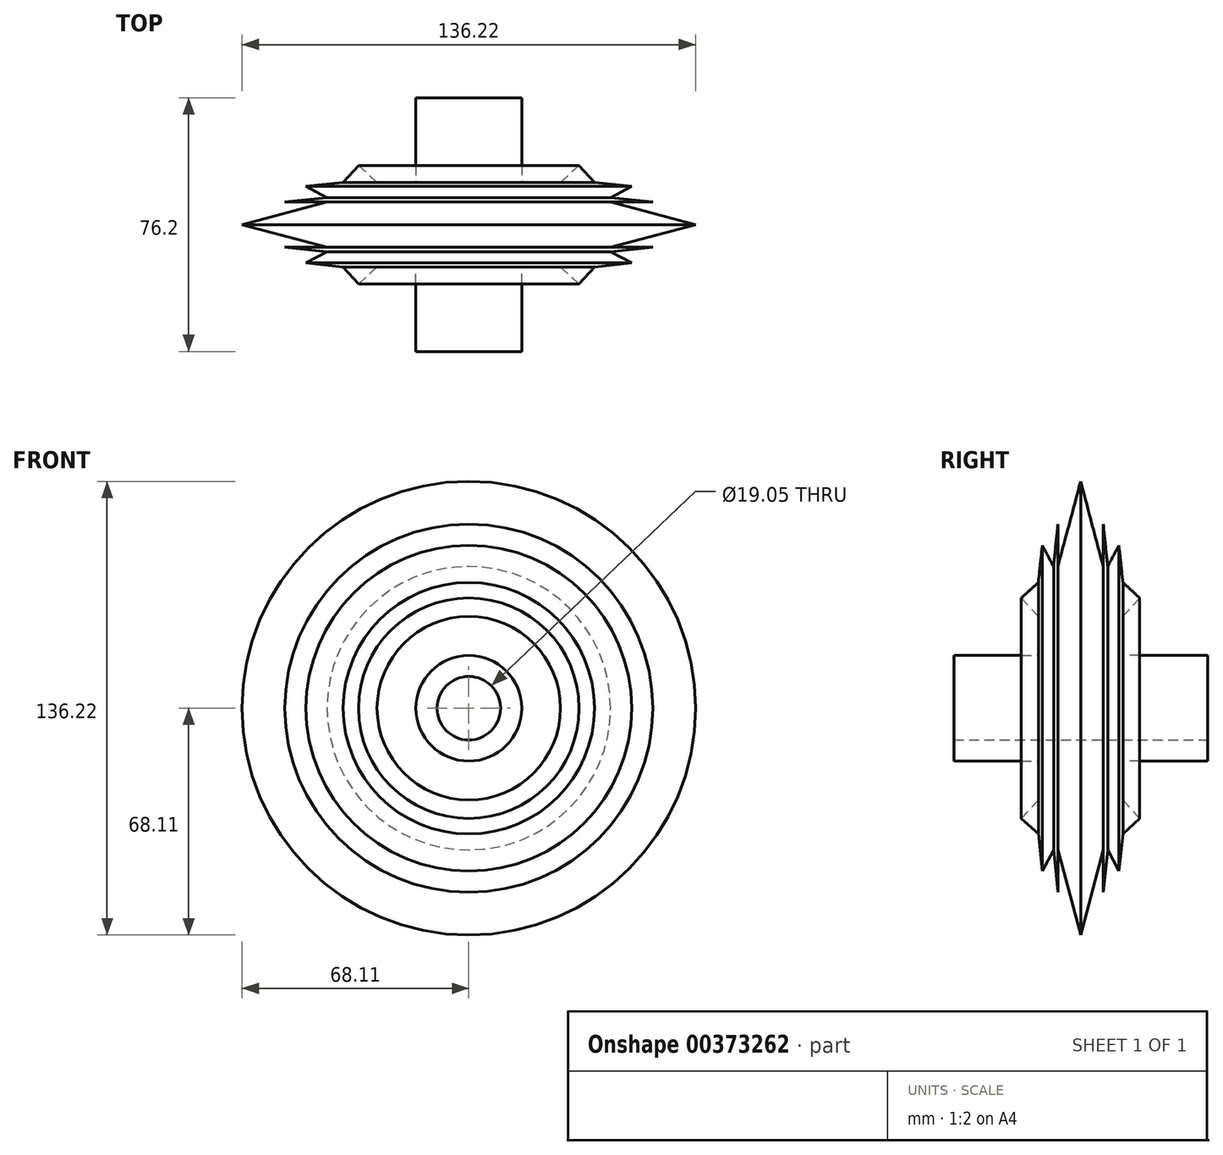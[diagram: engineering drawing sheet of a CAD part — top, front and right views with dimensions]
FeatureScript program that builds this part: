
annotation { "Feature Type Name" : "Feature", "Feature Type Description" : "" }
export const myFeature = defineFeature(function(context is Context, id is Id, definition is map)
    precondition{}
    {
        {
            var Q0;
            Q0=qCreatedBy(makeId("Front.planeOp"),FACE);
            var sketch = newSketch(context, id + "F0", { "sketchPlane" : qUnion([Q0])});
            skCircle(sketch, "E0", {"center": v(0, 0) * mm, "radius": 9.53 * mm});
            skCircle(sketch, "E1", {"center": v(0, 0) * mm, "radius": 15.88 * mm});
            skSolve(sketch);
        }
        {
            var Q0;
            Q0=makeQuery(id+"F0.imprint","IMPRINT",FACE,{"disambiguationData":[TD([[makeQuery(id+"F0.imprint","IMPRINT",EDGE,{"derivedFrom":sQuery(id+"F0.wireOp",EDGE,"E0")}),-1.0]])]});
            extrude(context, id + "F1", {"entities" : qUnion([Q0]), "depth" : 25.4 * mm});
        }
        {
            var Q0;
            Q0=qCreatedBy(makeId("Right.planeOp"),FACE);
            var sketch = newSketch(context, id + "F2", { "sketchPlane" : qUnion([Q0])});
            skLineSegment(sketch, "E2", {"start": v(-25.4, 15.88) * mm, "end": v(-25.4, -15.87) * mm});
            skLineSegment(sketch, "E3", {"start": v(-25.4, 15.87) * mm, "end": v(0, 15.87) * mm});
            skLineSegment(sketch, "E4", {"start": v(0, 15.87) * mm, "end": v(0, -16.16) * mm});
            skLineSegment(sketch, "E5", {"start": v(0, -16.16) * mm, "end": v(-25.4, -15.87) * mm});
            skLineSegment(sketch, "E6", {"start": v(0, -16.16) * mm, "end": v(0, 15.87) * mm});
            skLineSegment(sketch, "E7", {"start": v(-25.4, 9.85) * mm, "end": v(0, 9.85) * mm});
            skLineSegment(sketch, "E8", {"start": v(-25.4, 33.1) * mm, "end": v(-25.4, 9.85) * mm});
            skLineSegment(sketch, "E9", {"start": v(0, 33.1) * mm, "end": v(5.08, 33.1) * mm});
            skLineSegment(sketch, "E10", {"start": v(-25.4, 33.1) * mm, "end": v(-30.48, 33.1) * mm});
            skLineSegment(sketch, "E11", {"start": v(-30.48, 33.1) * mm, "end": v(-25.4, 37.76) * mm});
            skLineSegment(sketch, "E12", {"start": v(-25.4, 37.76) * mm, "end": v(-25.4, 33.1) * mm});
            skLineSegment(sketch, "E13", {"start": v(-30.48, 33.1) * mm, "end": v(-25.4, 27.56) * mm});
            skLineSegment(sketch, "E14", {"start": v(-25.4, 37.76) * mm, "end": v(-20.83, 42.57) * mm});
            skLineSegment(sketch, "E15", {"start": v(-20.83, 42.57) * mm, "end": v(-4.57, 42.57) * mm});
            skLineSegment(sketch, "E16", {"start": v(-20.83, 42.57) * mm, "end": v(-19.5, 55.27) * mm});
            skLineSegment(sketch, "E17", {"start": v(-19.5, 55.27) * mm, "end": v(-19.5, 42.57) * mm});
            skLineSegment(sketch, "E18", {"start": v(-20.83, 42.57) * mm, "end": v(-24.2, 48.92) * mm});
            skPoint(sketch, "E18.endSnap0", {"position": v(-20.17, 48.92) * mm});
            skLineSegment(sketch, "E19", {"start": v(-24.2, 48.92) * mm, "end": v(-25.4, 37.76) * mm});
            skLineSegment(sketch, "E20", {"start": v(-12.7, 42.57) * mm, "end": v(-12.7, 15.87) * mm});
            skLineSegment(sketch, "E21", {"start": v(-19.5, 42.57) * mm, "end": v(-12.7, 68.11) * mm});
            skLineSegment(sketch, "E22", {"start": v(-12.7, 42.57) * mm, "end": v(-12.7, 68.11) * mm});
            skLineSegment(sketch, "E23.MirrorCS", {"start": v(-5.9, 42.57) * mm, "end": v(-12.7, 68.11) * mm});
            skLineSegment(sketch, "E24.MirrorCS", {"start": v(-5.9, 55.27) * mm, "end": v(-5.9, 42.57) * mm});
            skLineSegment(sketch, "E25.MirrorCS", {"start": v(-4.57, 42.57) * mm, "end": v(-5.9, 55.27) * mm});
            skLineSegment(sketch, "E26.MirrorCS", {"start": v(-4.57, 42.57) * mm, "end": v(-1.2, 48.92) * mm});
            skLineSegment(sketch, "E27.MirrorCS", {"start": v(-1.2, 48.92) * mm, "end": v(0, 37.76) * mm});
            skLineSegment(sketch, "E28.MirrorCS", {"start": v(5.08, 33.1) * mm, "end": v(0, 37.76) * mm});
            skLineSegment(sketch, "E29.MirrorCS", {"start": v(5.08, 33.1) * mm, "end": v(0, 27.56) * mm});
            skLineSegment(sketch, "E30.MirrorCS", {"start": v(0, 33.1) * mm, "end": v(0, 9.85) * mm});
            skLineSegment(sketch, "E31.MirrorCS", {"start": v(0, 37.76) * mm, "end": v(0, 33.1) * mm});
            skSolve(sketch);
        }
        {
            var Q0;
            {var subQ0=sQuery(id+"F2.wireOp",EDGE,"E12");Q0=makeQuery(id+"F2.imprint","IMPRINT",FACE,{"disambiguationData":[TD([[makeQuery(id+"F2.imprint","IMPRINT",EDGE,{"derivedFrom":subQ0}),1.0]])]});}
            var Q1;
            {var subQ0=sQuery(id+"F2.wireOp",EDGE,"E20");Q1=makeQuery(id+"F2.imprint","IMPRINT",FACE,{"disambiguationData":[TD([[makeQuery(id+"F2.imprint","IMPRINT",EDGE,{"derivedFrom":subQ0}),1.0]])]});}
            var Q2;
            {var subQ0=sQuery(id+"F2.wireOp",EDGE,"E9");Q2=makeQuery(id+"F2.imprint","IMPRINT",FACE,{"disambiguationData":[TD([[makeQuery(id+"F2.imprint","IMPRINT",EDGE,{"derivedFrom":subQ0}),-1.0]])]});}
            var Q3;
            Q3=makeQuery(id+"F2.imprint","IMPRINT",FACE,{"disambiguationData":[TD([[makeQuery(id+"F2.imprint","IMPRINT",EDGE,{"derivedFrom":sQuery(id+"F2.wireOp",EDGE,"E9")}),1.0]])]});
            var Q4;
            {var subQ0=sQuery(id+"F2.wireOp",EDGE,"E10");Q4=makeQuery(id+"F2.imprint","IMPRINT",FACE,{"disambiguationData":[TD([[makeQuery(id+"F2.imprint","IMPRINT",EDGE,{"derivedFrom":subQ0}),1.0]])]});}
            var Q5;
            Q5=makeQuery(id+"F2.imprint","IMPRINT",FACE,{"disambiguationData":[TD([[makeQuery(id+"F2.imprint","IMPRINT",EDGE,{"derivedFrom":sQuery(id+"F2.wireOp",EDGE,"E10")}),-1.0]])]});
            var Q6;
            Q6=makeQuery(id+"F2.imprint","IMPRINT",FACE,{"disambiguationData":[TD([[makeQuery(id+"F2.imprint","IMPRINT",EDGE,{"derivedFrom":sQuery(id+"F2.wireOp",EDGE,"E14")}),1.0]])]});
            var Q7;
            {var subQ0=sQuery(id+"F2.wireOp",EDGE,"E16");Q7=makeQuery(id+"F2.imprint","IMPRINT",FACE,{"disambiguationData":[TD([[makeQuery(id+"F2.imprint","IMPRINT",EDGE,{"derivedFrom":subQ0}),-1.0]])]});}
            var Q8;
            {var subQ0=sQuery(id+"F2.wireOp",EDGE,"E21");Q8=makeQuery(id+"F2.imprint","IMPRINT",FACE,{"disambiguationData":[TD([[makeQuery(id+"F2.imprint","IMPRINT",EDGE,{"derivedFrom":subQ0}),-1.0]])]});}
            var Q9;
            {var subQ0=sQuery(id+"F2.wireOp",EDGE,"E22");Q9=makeQuery(id+"F2.imprint","IMPRINT",FACE,{"disambiguationData":[TD([[makeQuery(id+"F2.imprint","IMPRINT",EDGE,{"derivedFrom":subQ0}),-1.0]])]});}
            var Q10;
            {var subQ2=sQuery(id+"F2.wireOp",EDGE,"E24.MirrorCS");Q10=makeQuery(id+"F2.imprint","IMPRINT",FACE,{"disambiguationData":[TD([[makeQuery(id+"F2.imprint","IMPRINT",EDGE,{"derivedFrom":subQ2}),1.0]])]});}
            var Q11;
            Q11=makeQuery(id+"F1.opExtrude","SWEPT_FACE",FACE,{"disambiguationData":[OSD([sQuery(id+"F0.wireOp",EDGE,"E0")])]});
            revolve(context, id + "F3", {"operationType" : NewBodyOperationType.ADD, "entities" : qUnion([Q0, Q1, Q2, Q3, Q4, Q5, Q6, Q7, Q8, Q9, Q10]), "axis" : qUnion([Q11]), "revolveType" : RevolveType.FULL});
        }
        {
            var Q0;
            Q0=makeQuery(id+"F0.imprint","IMPRINT",FACE,{"disambiguationData":[TD([[makeQuery(id+"F0.imprint","IMPRINT",EDGE,{"derivedFrom":sQuery(id+"F0.wireOp",EDGE,"E0")}),-1.0]])]});
            extrude(context, id + "F4", {"entities" : qUnion([Q0]), "operationType" : NewBodyOperationType.ADD, "depth" : 50.8 * mm});
        }
        {
            var Q0;
            Q0=makeQuery(id+"F0.imprint","IMPRINT",FACE,{"disambiguationData":[TD([[makeQuery(id+"F0.imprint","IMPRINT",EDGE,{"derivedFrom":sQuery(id+"F0.wireOp",EDGE,"E0")}),-1.0]])]});
            extrude(context, id + "F5", {"entities" : qUnion([Q0]), "operationType" : NewBodyOperationType.ADD, "oppositeDirection" : true, "depth" : 25.4 * mm});
        }
    });
